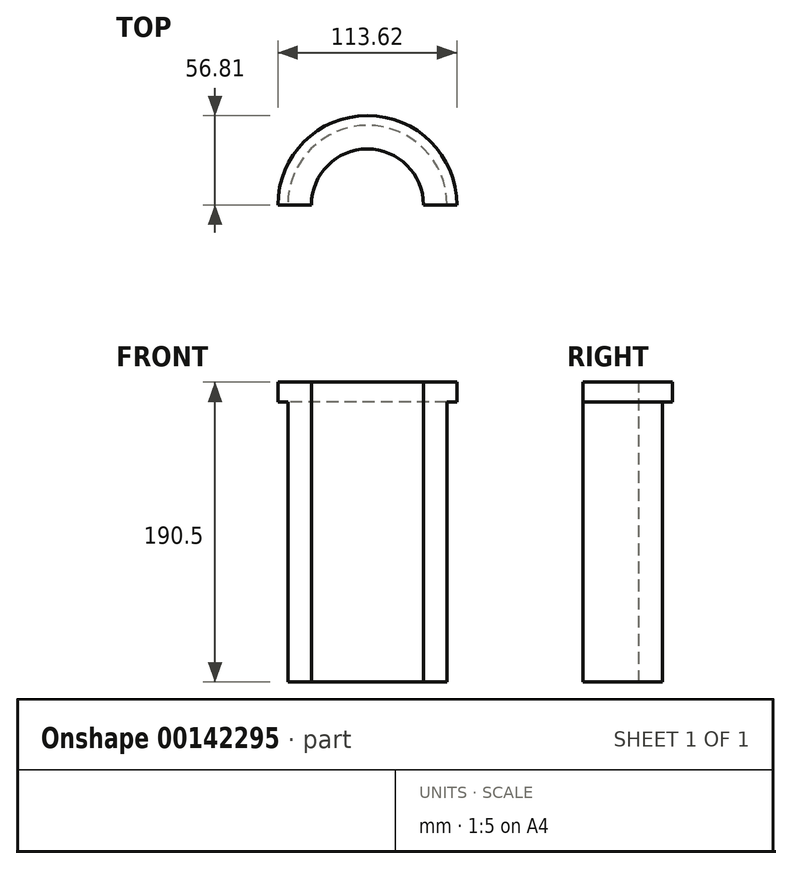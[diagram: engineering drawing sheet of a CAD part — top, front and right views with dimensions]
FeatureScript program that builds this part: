
annotation { "Feature Type Name" : "Feature", "Feature Type Description" : "" }
export const myFeature = defineFeature(function(context is Context, id is Id, definition is map)
    precondition{}
    {
        {
            var Q0;
            Q0=qCreatedBy(makeId("Top.planeOp"),FACE);
            var sketch = newSketch(context, id + "F0", { "sketchPlane" : qUnion([Q0])});
            skCircle(sketch, "E0", {"center": v(0, 0) * mm, "radius": 56.81 * mm});
            skSolve(sketch);
        }
        {
            var Q0;
            Q0 = qSketchRegion(id + "F0", true);
            extrude(context, id + "F1", {"entities" : qUnion([Q0]), "depth" : 12.7 * mm});
        }
        {
            var Q0;
            Q0=makeQuery(id+"F1.opExtrude","CAP_FACE",FACE,{"disambiguationData":[OSD([sQuery(id+"F0.wireOp",EDGE,"E0")])],"isStart":true});
            var sketch = newSketch(context, id + "F2", { "sketchPlane" : qUnion([Q0])});
            skCircle(sketch, "E1", {"center": v(0, 0) * mm, "radius": 50.53 * mm});
            skSolve(sketch);
        }
        {
            var Q0;
            Q0 = qSketchRegion(id + "F2", true);
            extrude(context, id + "F3", {"entities" : qUnion([Q0]), "operationType" : NewBodyOperationType.ADD, "depth" : 177.8 * mm});
        }
        {
            var Q0;
            Q0=makeQuery(id+"F1.opExtrude","CAP_FACE",FACE,{"disambiguationData":[OSD([sQuery(id+"F0.wireOp",EDGE,"E0")])],"isStart":false});
            var sketch = newSketch(context, id + "F4", { "sketchPlane" : qUnion([Q0])});
            skCircle(sketch, "E2", {"center": v(0, 0) * mm, "radius": 35.56 * mm});
            skSolve(sketch);
        }
        {
            var Q0;
            Q0 = qSketchRegion(id + "F4", true);
            extrude(context, id + "F5", {"entities" : qUnion([Q0]), "operationType" : NewBodyOperationType.REMOVE, "oppositeDirection" : true, "depth" : 203.2 * mm});
        }
        {
            var Q0;
            Q0=qCreatedBy(makeId("Top.planeOp"),FACE);
            var sketch = newSketch(context, id + "F6", { "sketchPlane" : qUnion([Q0])});
            skLineSegment(sketch, "E3.bottom", {"start": v(69.03, 0) * mm, "end": v(-64.54, 0) * mm});
            skLineSegment(sketch, "E3.top", {"start": v(69.03, -62.38) * mm, "end": v(-64.54, -62.38) * mm});
            skLineSegment(sketch, "E3.left", {"start": v(-64.54, 0) * mm, "end": v(-64.54, -62.38) * mm});
            skLineSegment(sketch, "E3.right", {"start": v(69.03, 0) * mm, "end": v(69.03, -62.38) * mm});
            skSolve(sketch);
        }
        {
            var Q0;
            Q0 = qSketchRegion(id + "F6", true);
            extrude(context, id + "F7", {"entities" : qUnion([Q0]), "operationType" : NewBodyOperationType.REMOVE, "oppositeDirection" : true, "depth" : 203.2 * mm, "hasSecondDirection" : true, "secondDirectionOppositeDirection" : false, "secondDirectionDepth" : 25.4 * mm});
        }
    });
